# Revit family: Storage-Mounted-Teknion-BCLOO_Cubic_Open_Tower_Low_Secondary_Desk-R2018
name_source: partatom
category: Furniture
revit_build: Autodesk Revit 2018 (Build: 20170223_1515(x64)
units: mm (PartAtom-declared; Revit-internal decimal feet)

## family parameters
Always vertical = Yes
Cut with Voids When Loaded = No
OmniClass Number = 23.40.20.00
OmniClass Title = General Furniture and Specialties
Room Calculation Point = No
Shared = Yes
Work Plane-Based = No

## types (4) — shared parameters
Assembly Code = E2020200
Manufacturer = Teknion
Manufacturer Fax = 416.661.4586
Part Number = BCLOO
Product Documentation Link = https://www.teknion.com
Product Line = Expansion Casegoods
Product Page URL = https://www.teknion.com
Series = Expansion Casegoods
Sustainability Data = https://www.teknion.com
URL = www.teknion.com
Unit Weight URL = http://www.teknion.com
Warranty = http://www.teknion.com

## per-type parameters (varying)
| type | Actual Height | Actual Width | Bottom Shelf Height Offset | Description | Middle Shelf Divider | Model | Top Shelf Height Offset |
| 18" Depth, 18" Width, 66" Height | 65.374 " | 17.91 " | 16.445 " | Cubic Open Tower - Low Secondary Desk Mounted, 18" Depth, 18" Width, 66" Height | No | BCLOO181866 | 15.606 " |
| 18" Depth, 18" Width, 72" Height | 71.626 " | 17.91 " | 18.529 " | Cubic Open Tower - Low Secondary Desk Mounted, 18" Depth, 18" Width, 72" Height | No | BCLOO181872 | 17.69 " |
| 18" Depth, 36" Width, 66" Height | 65.374 " | 35.82 " | 16.445 " | Cubic Open Tower - Low Secondary Desk Mounted, 18" Depth, 36" Width, 66" Height | Yes | BCLOO183666 | 15.606 " |
| 18" Depth, 36" Width, 72" Height | 71.626 " | 35.82 " | 18.529 " | Cubic Open Tower - Low Secondary Desk Mounted, 18" Depth, 36" Width, 72" Height | Yes | BCLOO183672 | 17.69 " |

## geometry (parser evidence)
native form markers: Sweep x2
no freeform markers — native parametric forms only
